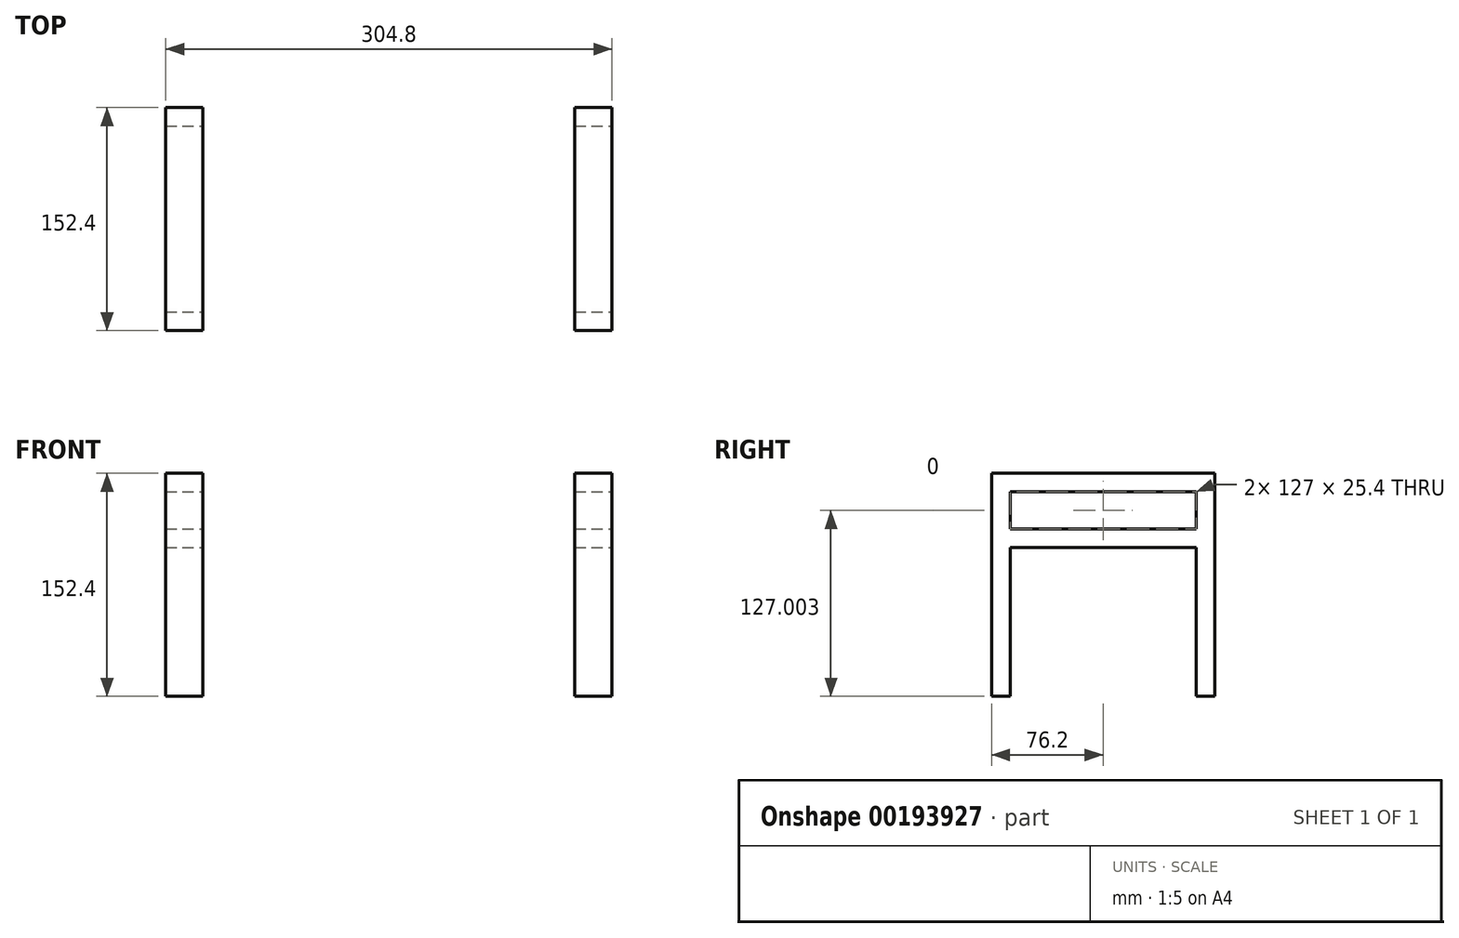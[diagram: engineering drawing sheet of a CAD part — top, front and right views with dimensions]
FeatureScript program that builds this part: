
annotation { "Feature Type Name" : "Feature", "Feature Type Description" : "" }
export const myFeature = defineFeature(function(context is Context, id is Id, definition is map)
    precondition{}
    {
        {
            var Q0;
            Q0=qCreatedBy(makeId("Front.planeOp"),FACE);
            var sketch = newSketch(context, id + "F0", { "sketchPlane" : qUnion([Q0])});
            skLineSegment(sketch, "E0.bottom", {"start": v(-152.48, -0.73) * mm, "end": v(152.32, -0.73) * mm});
            skLineSegment(sketch, "E0.top", {"start": v(-152.48, -153.13) * mm, "end": v(152.32, -153.13) * mm});
            skLineSegment(sketch, "E0.left", {"start": v(-152.48, -0.73) * mm, "end": v(-152.48, -153.13) * mm});
            skLineSegment(sketch, "E0.right", {"start": v(152.32, -0.73) * mm, "end": v(152.32, -153.13) * mm});
            skSolve(sketch);
        }
        {
            var Q0;
            Q0 = qSketchRegion(id + "F0", true);
            extrude(context, id + "F1", {"entities" : qUnion([Q0]), "depth" : 152.4 * mm});
        }
        {
            var Q0;
            Q0=makeQuery(id+"F1.opExtrude","SWEPT_FACE",FACE,{"disambiguationData":[OSD([sQuery(id+"F0.wireOp",EDGE,"E0.right")])]});
            var sketch = newSketch(context, id + "F2", { "sketchPlane" : qUnion([Q0])});
            skLineSegment(sketch, "E1.0", {"start": v(-139.7, -0.73) * mm, "end": v(-139.7, -153.13) * mm});
            skLineSegment(sketch, "E2.0", {"start": v(-152.4, -13.43) * mm, "end": v(0, -13.43) * mm});
            skLineSegment(sketch, "E3.0", {"start": v(-12.7, -0.73) * mm, "end": v(-12.7, -153.13) * mm});
            skLineSegment(sketch, "E4.0", {"start": v(-152.4, -38.83) * mm, "end": v(0, -38.83) * mm});
            skLineSegment(sketch, "E5.0", {"start": v(-152.4, -51.53) * mm, "end": v(0, -51.53) * mm});
            skLineSegment(sketch, "E6.0", {"start": v(-6.35, -146.78) * mm, "end": v(-6.35, -7.08) * mm});
            skLineSegment(sketch, "E6.2", {"start": v(-146.05, -7.08) * mm, "end": v(-146.05, -146.78) * mm});
            skLineSegment(sketch, "E6.3", {"start": v(-6.35, -7.08) * mm, "end": v(-146.05, -7.08) * mm});
            skSolve(sketch);
        }
        {
            var Q0;
            {var subQ0=sQuery(id+"F2.wireOp",EDGE,"E1.0");var subQ3=sQuery(id+"F2.wireOp",EDGE,"E5.0");var subQ4=makeQuery(id+"F2.imprint","INTERSECT",VERTEX,{"derivedFrom":[subQ0,subQ3]});Q0=makeQuery(id+"F2.imprint","IMPRINT",FACE,{"disambiguationData":[TD([[makeQuery(id+"F2.imprint","IMPRINT",EDGE,{"disambiguationData":[TD([[subQ4,-1.0]])],"derivedFrom":subQ3}),-1.0]])]});}
            var Q1;
            {var subQ0=sQuery(id+"F2.wireOp",EDGE,"E2.0");var subQ1=sQuery(id+"F2.wireOp",EDGE,"E1.0");var subQ2=makeQuery(id+"F2.imprint","INTERSECT",VERTEX,{"derivedFrom":[subQ1,subQ0]});Q1=makeQuery(id+"F2.imprint","IMPRINT",FACE,{"disambiguationData":[TD([[makeQuery(id+"F2.imprint","IMPRINT",EDGE,{"disambiguationData":[TD([[subQ2,-1.0]])],"derivedFrom":subQ1}),1.0]])]});}
            extrude(context, id + "F3", {"entities" : qUnion([Q0, Q1]), "operationType" : NewBodyOperationType.REMOVE, "oppositeDirection" : true, "depth" : 304.8 * mm});
        }
        {
            var Q0;
            Q0=makeQuery(id+"F1.opExtrude","SWEPT_FACE",FACE,{"disambiguationData":[OSD([sQuery(id+"F0.wireOp",EDGE,"E0.bottom")])]});
            var sketch = newSketch(context, id + "F4", { "sketchPlane" : qUnion([Q0])});
            skLineSegment(sketch, "E7.0", {"start": v(126.92, -152.4) * mm, "end": v(126.92, 0) * mm});
            skLineSegment(sketch, "E8.0", {"start": v(-127.08, -152.4) * mm, "end": v(-127.08, 0) * mm});
            skSolve(sketch);
        }
        {
            var Q0;
            Q0 = qSketchRegion(id + "F4", true);
            var Q1;
            {var subQ0=sQuery(id+"F4.wireOp",EDGE,"E7.0");Q1=makeQuery(id+"F4.imprint","IMPRINT",FACE,{"disambiguationData":[TD([[makeQuery(id+"F4.imprint","IMPRINT",EDGE,{"derivedFrom":subQ0}),1.0]])]});}
            extrude(context, id + "F5", {"entities" : qUnion([Q0, Q1]), "operationType" : NewBodyOperationType.REMOVE, "oppositeDirection" : true, "depth" : 152.4 * mm});
        }
    });
